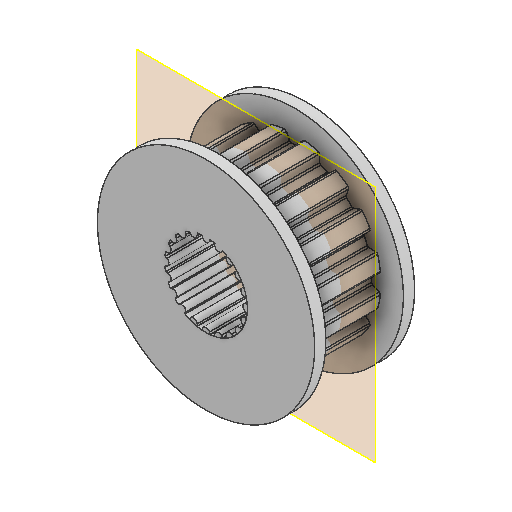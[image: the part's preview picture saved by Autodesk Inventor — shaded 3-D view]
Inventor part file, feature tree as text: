
AUTODESK INVENTOR PART (.ipt)
format: ipt  version: 2025.2 (Build 292293000, 293)  size: 684,544 bytes
history: native  units: in
note: dims shown in document units (in); Inventor stores cm internally (conversion verified against a paired STEP export)
features: sketch x5, extrude x4, plane x1
ambient origin geometry x8: Origin, YZ Plane, XZ Plane, XY Plane, X Axis, Y Axis, Z Axis, Center Point
bodies: Solid1 (feature_tree)
feature tree (10):
  extrude  "Extrusion1"  Depth=1.2402in
  plane  "Work Plane1"
  extrude  "Extrusion2"  [1 undecoded]
  extrude  "Extrusion3"  Depth=0.4429in TaperAngle=0.0deg
  extrude  "Extrusion5"  TaperAngle=0.0deg  [1 undecoded]
  sketch  "Sketch1"  dims[d0=0.4724in d1=1.2402in]
  sketch  "Sketch2"  dims[d5=0.9843in d6=0.4429in d7=0.0in]
  sketch  "Sketch3"  dims[d8=0.0in d9=0.0in]
  sketch  "Sketch Circular Pattern1"  dims[d2=0.5709in d3=0.0in d4=-0.2854in]
  sketch  "Sketch6"  dims[d12=0.5709in d13=0.0in d18=14.5669in d20=360.0deg d40=0.4429in d41=0.0in d45=0.9843in d46=0.0in d47=0.0in d48=0.0in d49=0.0in]
note: 2 required parameter values undecoded (feature->parameter linkage not recoverable at this tier; creation-order binding heuristic only, values carry confidence <= 0.55)
